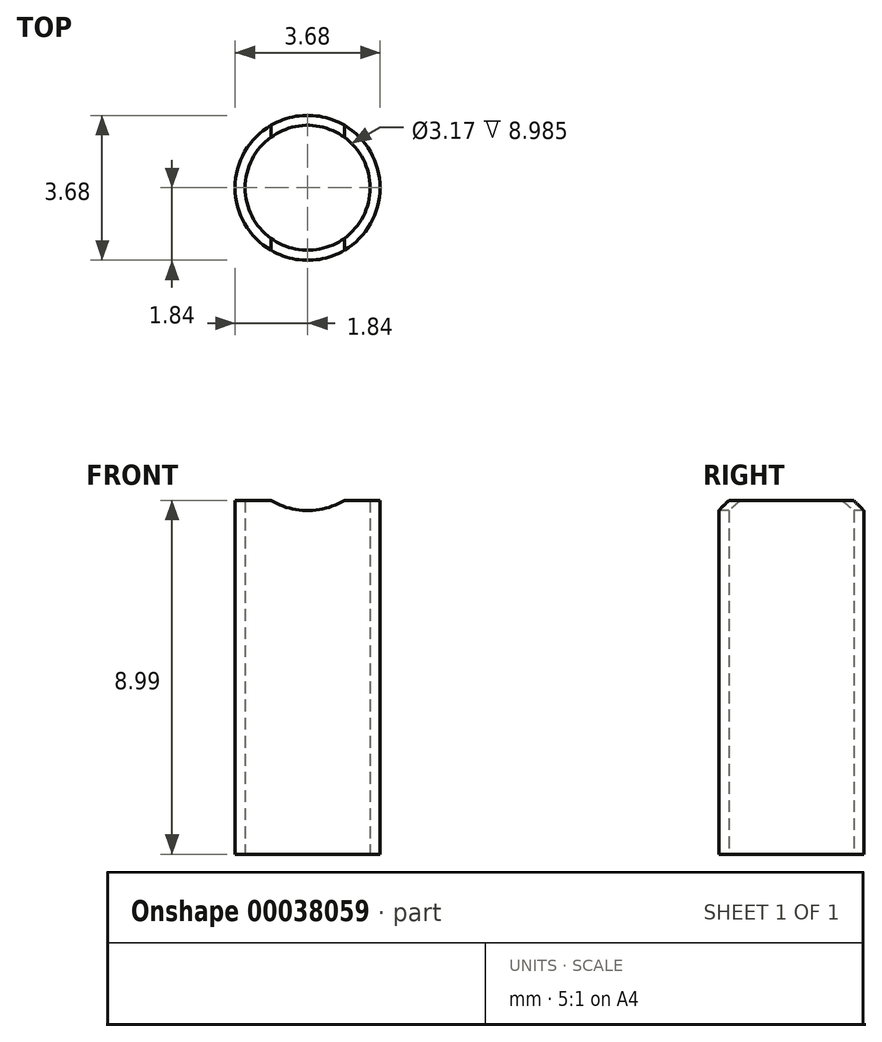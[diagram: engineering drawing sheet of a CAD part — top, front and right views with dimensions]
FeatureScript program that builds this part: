
annotation { "Feature Type Name" : "Feature", "Feature Type Description" : "" }
export const myFeature = defineFeature(function(context is Context, id is Id, definition is map)
    precondition{}
    {
        {
            var Q0;
            Q0=qCreatedBy(makeId("Top.planeOp"),FACE);
            var sketch = newSketch(context, id + "F0", { "sketchPlane" : qUnion([Q0])});
            skCircle(sketch, "E0", {"center": v(0, 0) * mm, "radius": 1.59 * mm});
            skLineSegment(sketch, "E1.rect.bottom", {"start": v(1.84, -1.84) * mm, "end": v(-1.84, -1.84) * mm});
            skLineSegment(sketch, "E1.rect.top", {"start": v(1.84, 1.84) * mm, "end": v(-1.84, 1.84) * mm});
            skLineSegment(sketch, "E1.rect.left", {"start": v(1.84, -1.84) * mm, "end": v(1.84, 1.84) * mm});
            skLineSegment(sketch, "E1.rect.right", {"start": v(-1.84, -1.84) * mm, "end": v(-1.84, 1.84) * mm});
            skSolve(sketch);
        }
        {
            var Q0;
            Q0 = qSketchRegion(id + "F0", true);
            extrude(context, id + "F1", {"entities" : qUnion([Q0]), "depth" : 9 * mm});
        }
        {
            var Q0;
            Q0=makeQuery(id+"F1.opExtrude","SWEPT_FACE",FACE,{"disambiguationData":[OSD([sQuery(id+"F0.wireOp",EDGE,"E1.rect.bottom")])]});
            var sketch = newSketch(context, id + "F2", { "sketchPlane" : qUnion([Q0])});
            skArc(sketch, "E2", {"start": v(-0.93, 8.99) * mm, "mid": v(0, 8.73) * mm, "end": v(0.93, 8.99) * mm});
            skLineSegment(sketch, "E3", {"start": v(-0.93, 8.99) * mm, "end": v(0.93, 8.99) * mm});
            skLineSegment(sketch, "E4", {"start": v(0, 8.73) * mm, "end": v(0, 8.99) * mm});
            skLineSegment(sketch, "E5", {"start": v(0, 8.99) * mm, "end": v(0, 10.57) * mm});
            skSolve(sketch);
        }
        {
            var Q0;
            Q0 = qSketchRegion(id + "F2", true);
            var Q1;
            Q1=makeQuery(id+"F1.opExtrude","SWEPT_FACE",FACE,{"disambiguationData":[OSD([sQuery(id+"F0.wireOp",EDGE,"E1.rect.top")])]});
            extrude(context, id + "F3", {"entities" : qUnion([Q0]), "operationType" : NewBodyOperationType.REMOVE, "endBound" : BoundingType.UP_TO_SURFACE, "oppositeDirection" : true, "endBoundEntityFace" : qUnion([Q1]), "depth" : 25.4 * mm});
        }
        {
            var Q0;
            Q0=makeQuery(id+"F1.opExtrude","SWEPT_EDGE",EDGE,{"disambiguationData":[OSD([sQuery(id+"F0.wireOp",EDGE,"E1.rect.bottom"),sQuery(id+"F0.wireOp",EDGE,"E1.rect.right")])]});
            var Q1;
            Q1=makeQuery(id+"F1.opExtrude","SWEPT_EDGE",EDGE,{"disambiguationData":[OSD([sQuery(id+"F0.wireOp",EDGE,"E1.rect.bottom"),sQuery(id+"F0.wireOp",EDGE,"E1.rect.left")])]});
            var Q2;
            Q2=makeQuery(id+"F1.opExtrude","SWEPT_EDGE",EDGE,{"disambiguationData":[OSD([sQuery(id+"F0.wireOp",EDGE,"E1.rect.top"),sQuery(id+"F0.wireOp",EDGE,"E1.rect.left")])]});
            var Q3;
            Q3=makeQuery(id+"F1.opExtrude","SWEPT_EDGE",EDGE,{"disambiguationData":[OSD([sQuery(id+"F0.wireOp",EDGE,"E1.rect.top"),sQuery(id+"F0.wireOp",EDGE,"E1.rect.right")])]});
            fillet(context, id + "F4", {"entities" : qUnion([Q0, Q1, Q2, Q3]), "radius" : 1.84 * mm, "tangentPropagation" : true, "allowEdgeOverflow" : false});
        }
    });
